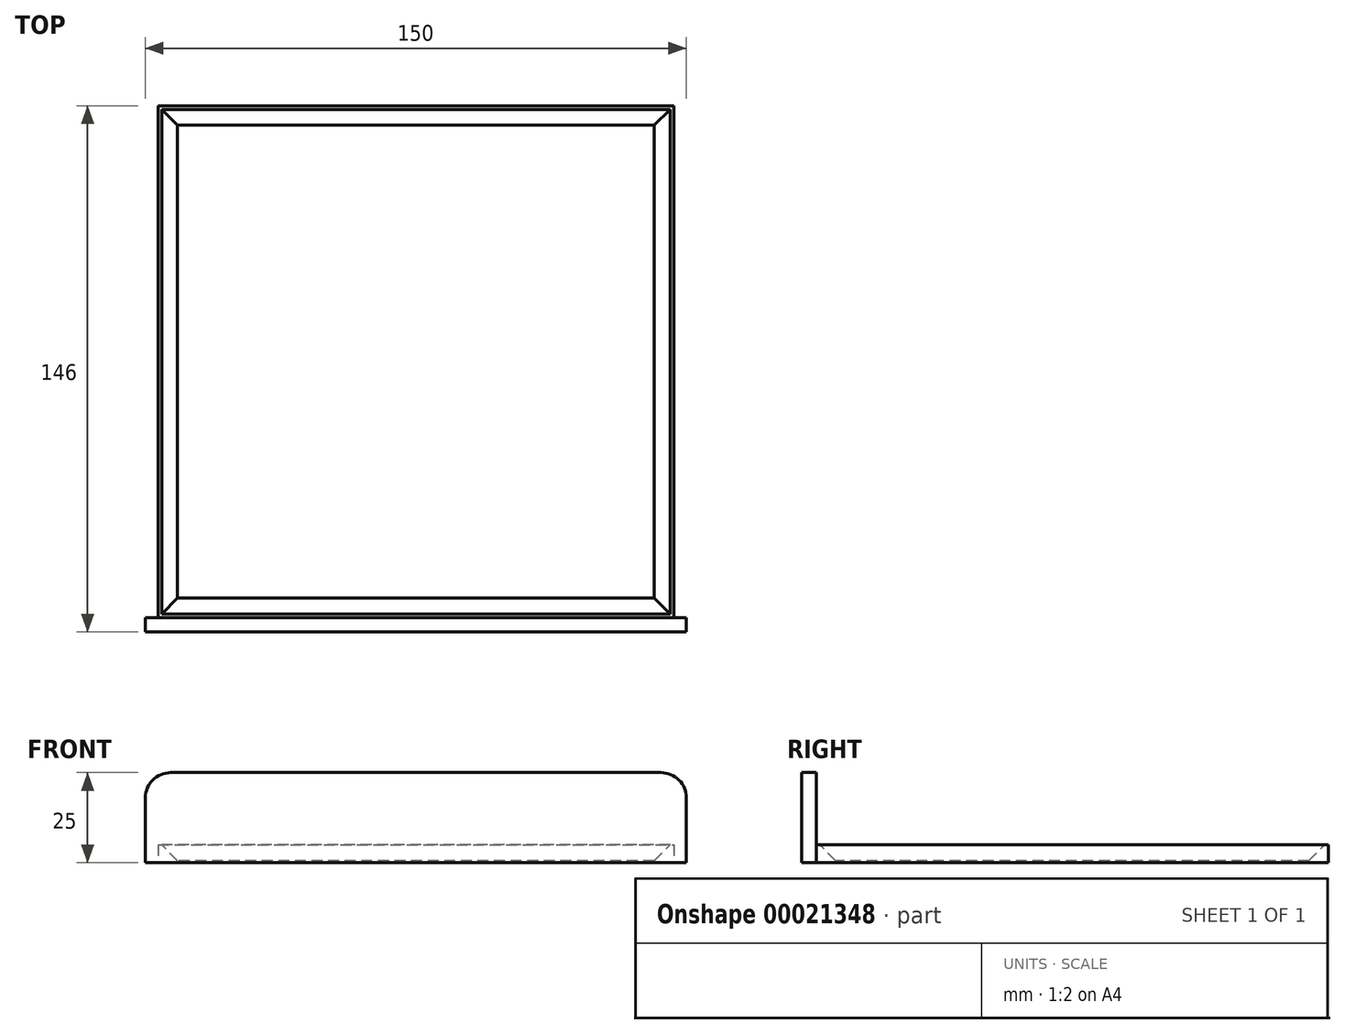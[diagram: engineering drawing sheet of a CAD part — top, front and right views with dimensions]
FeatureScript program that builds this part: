
annotation { "Feature Type Name" : "Feature", "Feature Type Description" : "" }
export const myFeature = defineFeature(function(context is Context, id is Id, definition is map)
    precondition{}
    {
        {
            var Q0;
            Q0=qCreatedBy(makeId("Top.planeOp"),FACE);
            var sketch = newSketch(context, id + "F0", { "sketchPlane" : qUnion([Q0])});
            skLineSegment(sketch, "E0.bottom", {"start": v(0, 0) * mm, "end": v(143, 0) * mm});
            skLineSegment(sketch, "E0.top", {"start": v(0, 142) * mm, "end": v(143, 142) * mm});
            skLineSegment(sketch, "E0.left", {"start": v(0, 0) * mm, "end": v(0, 142) * mm});
            skLineSegment(sketch, "E0.right", {"start": v(143, 0) * mm, "end": v(143, 142) * mm});
            skSolve(sketch);
        }
        {
            var Q0;
            Q0=makeQuery(id+"F0.imprint","IMPRINT",FACE,{"disambiguationData":[TD([[makeQuery(id+"F0.imprint","IMPRINT",EDGE,{"derivedFrom":sQuery(id+"F0.wireOp",EDGE,"E0.bottom")}),1.0]])]});
            extrude(context, id + "F1", {"entities" : qUnion([Q0]), "depth" : 5 * mm});
        }
        {
            var Q0;
            Q0=makeQuery(id+"F1.opExtrude","CAP_FACE",FACE,{"disambiguationData":[OSD([sQuery(id+"F0.wireOp",EDGE,"E0.bottom"),sQuery(id+"F0.wireOp",EDGE,"E0.top"),sQuery(id+"F0.wireOp",EDGE,"E0.left"),sQuery(id+"F0.wireOp",EDGE,"E0.right")])],"isStart":false});
            var sketch = newSketch(context, id + "F2", { "sketchPlane" : qUnion([Q0])});
            skLineSegment(sketch, "E1.0.0", {"start": v(0, 142) * mm, "end": v(0, 0) * mm});
            skLineSegment(sketch, "E1.0.1", {"start": v(0, 0) * mm, "end": v(143, 0) * mm});
            skLineSegment(sketch, "E1.0.2", {"start": v(143, 0) * mm, "end": v(143, 142) * mm});
            skLineSegment(sketch, "E1.0.3", {"start": v(143, 142) * mm, "end": v(0, 142) * mm});
            skLineSegment(sketch, "E2.0", {"start": v(1, 141) * mm, "end": v(1, 1) * mm});
            skLineSegment(sketch, "E2.1", {"start": v(142, 141) * mm, "end": v(1, 141) * mm});
            skLineSegment(sketch, "E2.2", {"start": v(142, 1) * mm, "end": v(142, 141) * mm});
            skLineSegment(sketch, "E2.3", {"start": v(1, 1) * mm, "end": v(142, 1) * mm});
            skSolve(sketch);
        }
        {
            var Q0;
            Q0=makeQuery(id+"F2.imprint","IMPRINT",FACE,{"disambiguationData":[TD([[makeQuery(id+"F2.imprint","IMPRINT",EDGE,{"derivedFrom":sQuery(id+"F2.wireOp",EDGE,"E2.0")}),1.0]])]});
            extrude(context, id + "F3", {"entities" : qUnion([Q0]), "operationType" : NewBodyOperationType.REMOVE, "oppositeDirection" : true, "depth" : 4.4 * mm, "hasDraft" : true, "draftAngle" : 45 * degree, "draftPullDirection" : true});
        }
        {
            var Q0;
            Q0=makeQuery(id+"F1.opExtrude","SWEPT_FACE",FACE,{"disambiguationData":[OSD([sQuery(id+"F0.wireOp",EDGE,"E0.bottom")])]});
            var sketch = newSketch(context, id + "F4", { "sketchPlane" : qUnion([Q0])});
            skLineSegment(sketch, "E3.bottom", {"start": v(-3.5, 0) * mm, "end": v(146.5, 0) * mm});
            skLineSegment(sketch, "E3.top", {"start": v(-3.5, 25) * mm, "end": v(146.5, 25) * mm});
            skLineSegment(sketch, "E3.left", {"start": v(-3.5, 0) * mm, "end": v(-3.5, 25) * mm});
            skLineSegment(sketch, "E3.right", {"start": v(146.5, 0) * mm, "end": v(146.5, 25) * mm});
            skLineSegment(sketch, "E4.0", {"start": v(0, 5) * mm, "end": v(143, 5) * mm, "construction": true});
            skPoint(sketch, "E5", {"position": v(71.5, 5) * mm});
            skPoint(sketch, "E6", {"position": v(71.5, 0) * mm});
            skLineSegment(sketch, "E7", {"start": v(71.5, 5) * mm, "end": v(71.5, 0) * mm, "construction": true});
            skSolve(sketch);
        }
        {
            var Q0;
            Q0=makeQuery(id+"F4.imprint","IMPRINT",FACE,{"disambiguationData":[TD([[makeQuery(id+"F4.imprint","IMPRINT",EDGE,{"derivedFrom":sQuery(id+"F4.wireOp",EDGE,"E3.top")}),-1.0]])]});
            var Q1;
            {var subQ0=sQuery(id+"F0.wireOp",EDGE,"E0.bottom");Q1=makeQuery(id+"F4.imprint","IMPRINT",FACE,{"disambiguationData":[TD([[makeQuery(id+"F4.imprint","IMPRINT",EDGE,{"derivedFrom":makeQuery(id+"F1.opExtrude","CAP_EDGE",EDGE,{"disambiguationData":[OSD([subQ0])],"isStart":false})}),-1.0]])]});}
            extrude(context, id + "F5", {"entities" : qUnion([Q0, Q1]), "operationType" : NewBodyOperationType.ADD, "depth" : 4 * mm});
        }
        {
            var Q0;
            Q0=makeQuery(id+"F5.opExtrude","SWEPT_EDGE",EDGE,{"disambiguationData":[OSD([sQuery(id+"F4.wireOp",EDGE,"E3.top"),sQuery(id+"F4.wireOp",EDGE,"E3.left")])]});
            var Q1;
            Q1=makeQuery(id+"F5.opExtrude","SWEPT_EDGE",EDGE,{"disambiguationData":[OSD([sQuery(id+"F4.wireOp",EDGE,"E3.top"),sQuery(id+"F4.wireOp",EDGE,"E3.right")])]});
            fillet(context, id + "F6", {"entities" : qUnion([Q0, Q1]), "radius" : 7 * mm, "tangentPropagation" : true, "allowEdgeOverflow" : false});
        }
    });
